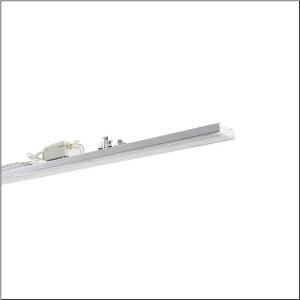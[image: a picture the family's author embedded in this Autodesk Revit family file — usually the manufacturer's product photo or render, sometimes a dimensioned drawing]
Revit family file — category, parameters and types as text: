
# Revit family: licross_21_recessed_ho_52tl11cn4c5s
name_source: partatom
category: Lighting Fixtures
units: mm (PartAtom-declared; Revit-internal decimal feet)

## family parameters
Cut with Voids When Loaded = No
Host = Face
Light Source = No
Part Type = Normal
Room Calculation Point = No
Round Connector Dimension = Use Diameter
Shared = No

## types (1)
- --- (1 x LED, 12640 lm, 68.4 W, 4000K)
    Apparent Load = 68 VA
    CIE Flux Codes = 87 95 99 100 100
    Color Rendering = 80
    Color Temperature = 4000K
    Default Elevation = 1800 mm
    Description = Licross 21 Recessed HO, luminaire insert, of sheet steel, galvanised, coil coated, white, length: 1.500mm, width: 66mm, height: 67mm, LED rated luminous flux: 12.640lm, light colour: 840, SDCM (Standard Deviation of Colour Matching)MacAdam ≤ 3 SDCM (initial), control gear: ON/OFF Multilumen, CLOi, with plug, 3-pole, with phase selection, mains connection: 220..240V, AC, 50/60Hz, start of lifetime: 68W, end of service life: 83W, internal wiring halogen-free, primary light control with lens, of plastic, primary optical cover: cover, of PMMA, light emission: direct distribution, primary light characteristic: symmetric, protection rating (complete): IP40, insulation class (complete): insulation class I (protective earthing), certification: CE, ENEC, VDE, UKCA, protection symbol: D if used in an environment without relevant dust loads with corresponding accessories, impact resistance: IK06, permissible ambient temperature for indoor applications: -35..+30°C, corresponds to IFS (International Featured Standards) requirements for safety and quality in the food industry, reducing of maximum allowable ambient temperature of 5°C with ceiling mounting, LABS conformity tested according to VDMA 24364:2018-05, The light source and the operating device comply with the requirements of the Ecodesign Regulation (EU) 2019/2020 and are replaceable in accordance with this regulation, packaging unit: 1 piece
    Height = 58 mm
    Lamp = 1 x LED
    Lamp Light Flux = 12640 lm
    Lamp Power = 68.4 W
    Lamp count = 1
    Length = 1500 mm
    Luminous efficacy = 185 lm/W
    Manufacturer = Siteco
    ModVariant = No
    Model = 52TL11CN4C5S
    Mounting Place = Ceiling
    Mounting Type = Pendant
    Number of Poles = 1
    OnlyDefault = Yes
    Power Factor = 1
    Product Name = Licross 21 Recessed HO
    Product group = luminaire insert | ceiling pendant
    ProductGroupID = 901
    Protection Class = Protection class I
    Protection Degree = IP 40
    RLX_Detail_Level = 1
    RLX_Emergency_Light_Flux = 0 lm
    RLX_Emergency_Type = 0
    RLX_Emergency_Type_DB = No
    RlxData = <blob elided: 22569 chars, md5=cb19fae0>
    Socket = socket
    Standby Power = 0 W
    System Light Flux = 12640 lm
    System Power = 68 W
    Type Comments = factory setting: luminous flux: 100 % | (A | C | E) | 161 mA
    Type Image = l_1296930.jpg
    URL = http://relux.com
    VarID = @adj_112221
    Voltage = 0 V
    Weight = 0.00 kg
    Width = 66 mm

## geometry (parser evidence)
native form markers: Blend x4, Sweep x11
no freeform markers — native parametric forms only
